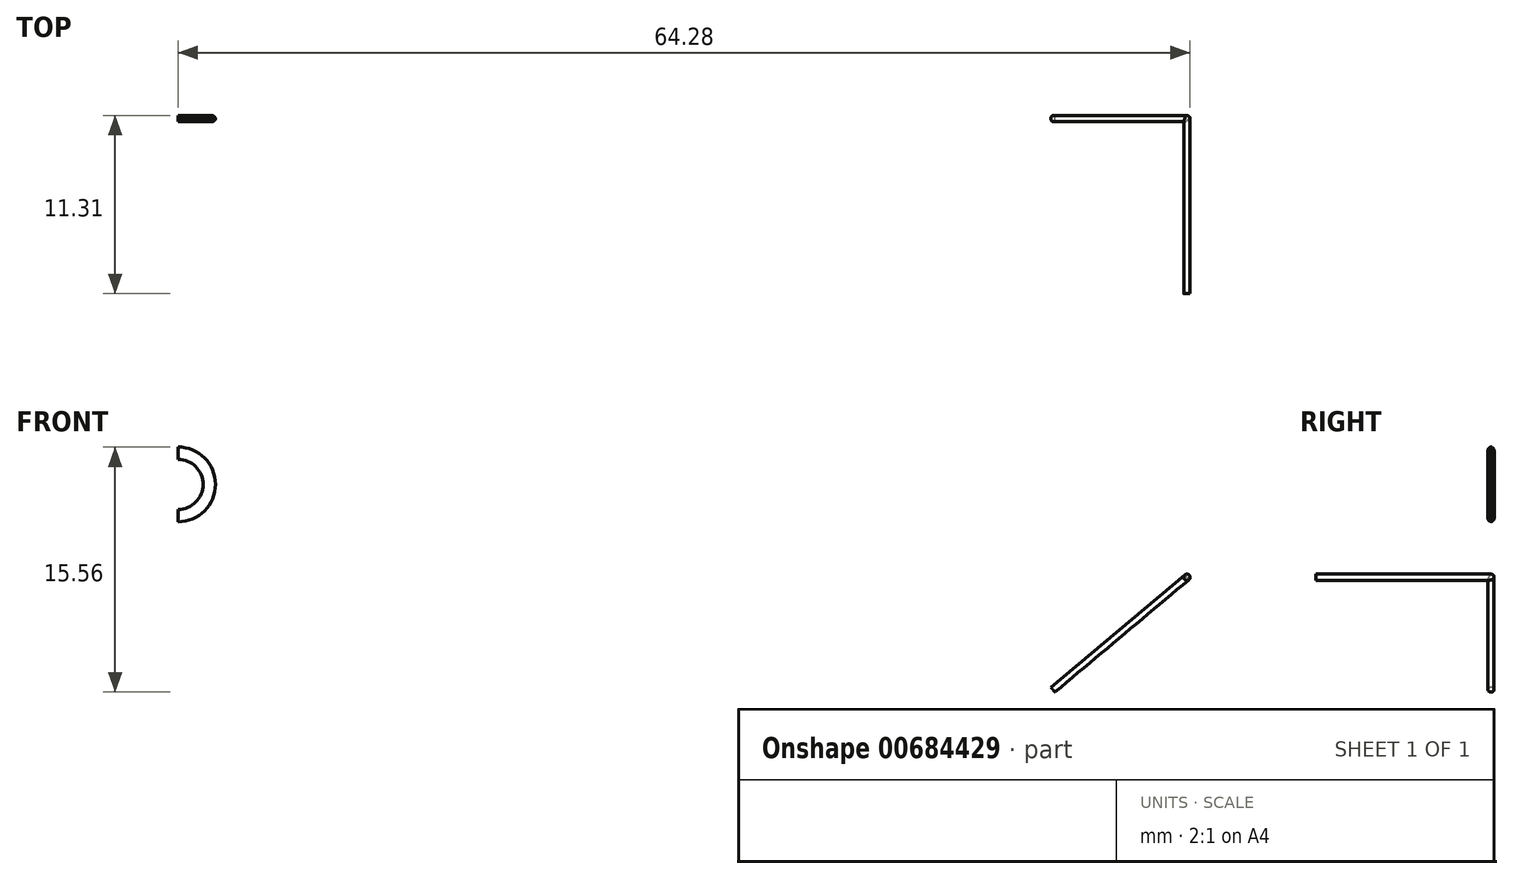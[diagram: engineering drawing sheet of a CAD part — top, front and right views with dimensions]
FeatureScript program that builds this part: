
annotation { "Feature Type Name" : "Feature", "Feature Type Description" : "" }
export const myFeature = defineFeature(function(context is Context, id is Id, definition is map)
    precondition{}
    {
        {
            var Q0;
            Q0=qCreatedBy(makeId("Front.planeOp"),FACE);
            var sketch = newSketch(context, id + "F0", { "sketchPlane" : qUnion([Q0])});
            skCircle(sketch, "E0", {"center": v(0, 0) * mm, "radius": 0.2 * mm});
            skSolve(sketch);
        }
        {
            var Q0;
            Q0=makeQuery(id+"F0.imprint","IMPRINT",FACE,{"disambiguationData":[TD([[makeQuery(id+"F0.imprint","IMPRINT",EDGE,{"derivedFrom":sQuery(id+"F0.wireOp",EDGE,"E0")}),1.0]])]});
            extrude(context, id + "F1", {"entities" : qUnion([Q0]), "depth" : 11.1 * mm, "offsetDistance" : 25.4 * mm});
        }
        {
            var Q0;
            Q0=qCreatedBy(makeId("Front.planeOp"),FACE);
            var sketch = newSketch(context, id + "F2", { "sketchPlane" : qUnion([Q0])});
            skLineSegment(sketch, "E1", {"start": v(0, 0) * mm, "end": v(55.38, 0) * mm});
            skLineSegment(sketch, "E2", {"start": v(0, 0) * mm, "end": v(-8.51, -7.14) * mm});
            skLineSegment(sketch, "E3", {"start": v(0, 0) * mm, "end": v(-0.13, 0.15) * mm});
            skLineSegment(sketch, "E4", {"start": v(-0.13, 0.15) * mm, "end": v(-8.64, -7) * mm});
            skLineSegment(sketch, "E5", {"start": v(-8.64, -7) * mm, "end": v(-8.51, -7.14) * mm});
            skLineSegment(sketch, "E6", {"start": v(-75.65, 0) * mm, "end": v(-75.65, 4.76) * mm});
            skCircle(sketch, "E7", {"center": v(-64.08, 5.9) * mm, "radius": 2.38 * mm});
            skCircle(sketch, "E8", {"center": v(-64.08, 5.9) * mm, "radius": 1.59 * mm});
            skLineSegment(sketch, "E9", {"start": v(-64.08, 3.52) * mm, "end": v(-64.08, 8.28) * mm});
            skSolve(sketch);
        }
        {
            var Q0;
            Q0=makeQuery(id+"F2.imprint","IMPRINT",FACE,{"disambiguationData":[TD([[makeQuery(id+"F2.imprint","IMPRINT",EDGE,{"derivedFrom":sQuery(id+"F2.wireOp",EDGE,"E2")}),-1.0]])]});
            var Q1;
            Q1=sQuery(id+"F2.wireOp",EDGE,"E2");
            revolve(context, id + "F3", {"entities" : qUnion([Q0]), "axis" : qUnion([Q1]), "revolveType" : RevolveType.FULL});
        }
        {
            var Q0;
            Q0=makeQuery(id+"F1.opExtrude","CAP_FACE",FACE,{"disambiguationData":[OSD([sQuery(id+"F0.wireOp",EDGE,"E0")])],"isStart":true});
            var sketch = newSketch(context, id + "F4", { "sketchPlane" : qUnion([Q0])});
            skLineSegment(sketch, "E10", {"start": v(-0.13, -0.15) * mm, "end": v(0.13, 0.15) * mm});
            skSolve(sketch);
        }
        {
            var Q0;
            {var subQ0=sQuery(id+"F4.wireOp",EDGE,"E10");Q0=makeQuery(id+"F4.imprint","IMPRINT",FACE,{"disambiguationData":[TD([[makeQuery(id+"F4.imprint","IMPRINT",EDGE,{"derivedFrom":subQ0}),1.0]])]});}
            var Q1;
            Q1=sQuery(id+"F4.wireOp",EDGE,"E10");
            revolve(context, id + "F5", {"operationType" : NewBodyOperationType.ADD, "entities" : qUnion([Q0]), "axis" : qUnion([Q1]), "revolveType" : RevolveType.FULL});
        }
        {
            var Q0;
            {var subQ0=sQuery(id+"F2.wireOp",EDGE,"E9");var subQ1=sQuery(id+"F2.wireOp",EDGE,"E7");var subQ2=makeQuery(id+"F2.imprint","INTERSECT",VERTEX,{"disambiguationData":[OD(0.0)],"derivedFrom":[subQ1,subQ0]});Q0=makeQuery(id+"F2.imprint","IMPRINT",FACE,{"disambiguationData":[TD([[makeQuery(id+"F2.imprint","IMPRINT",EDGE,{"disambiguationData":[TD([[subQ2,1.0]])],"derivedFrom":subQ1}),1.0]])]});}
            extrude(context, id + "F6", {"entities" : qUnion([Q0]), "depth" : 0.2 * mm, "offsetDistance" : 25.4 * mm, "hasSecondDirection" : true, "secondDirectionOppositeDirection" : true, "secondDirectionDepth" : 0.2 * mm});
        }
        {
            var Q0;
            Q0=makeQuery(id+"F6.opExtrude","CAP_EDGE",EDGE,{"disambiguationData":[OSD([sQuery(id+"F2.wireOp",EDGE,"E7")])],"isStart":false});
            var Q1;
            Q1=makeQuery(id+"F6.opExtrude","CAP_EDGE",EDGE,{"disambiguationData":[OSD([sQuery(id+"F2.wireOp",EDGE,"E7")])],"isStart":true});
            fillet(context, id + "F7", {"entities" : qUnion([Q0, Q1]), "radius" : 0.25 * mm, "tangentPropagation" : true, "allowEdgeOverflow" : false});
        }
    });
